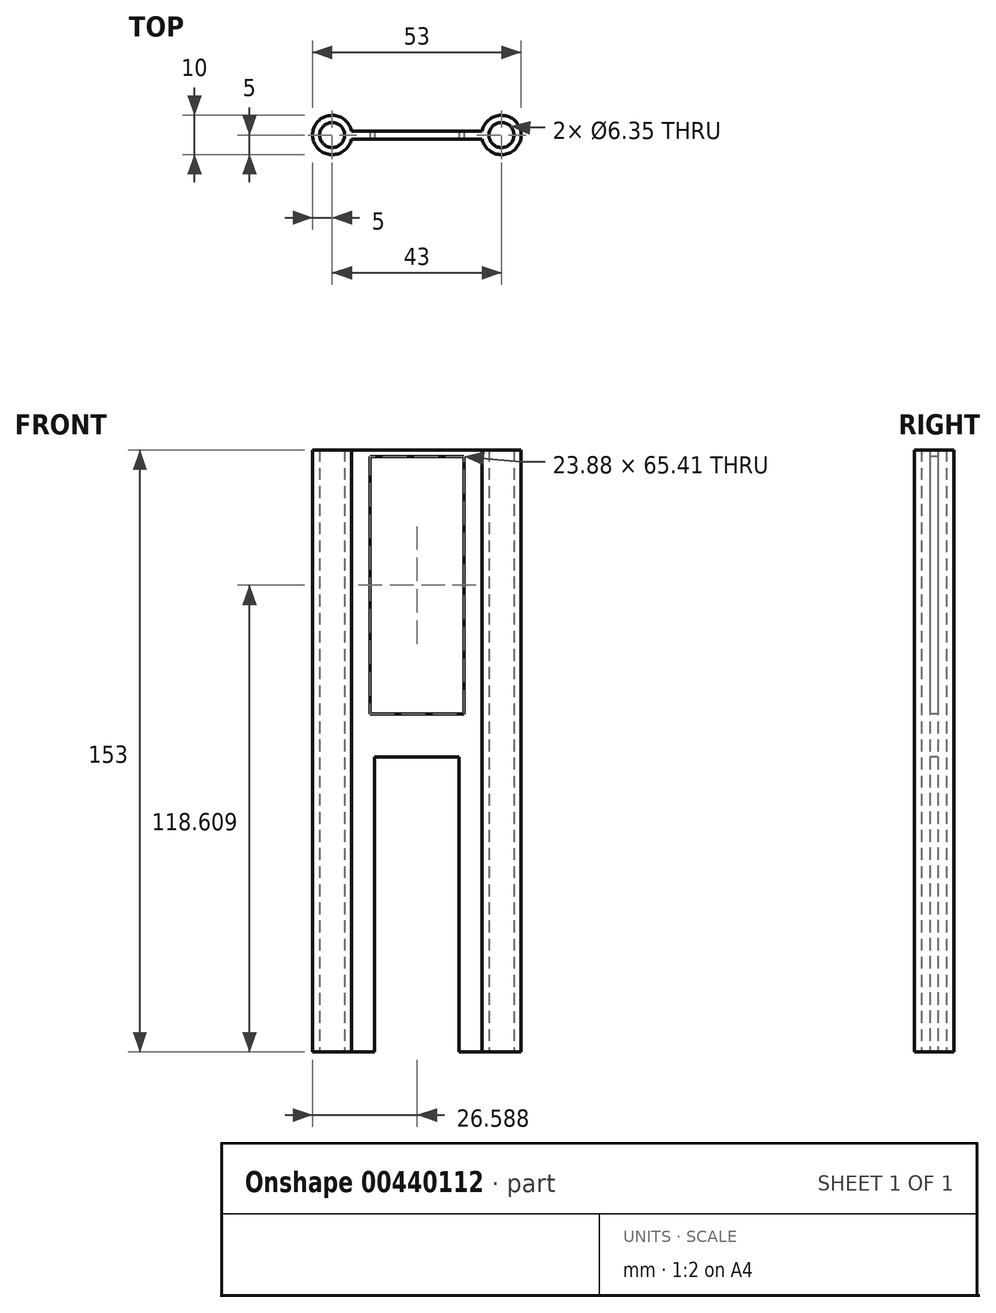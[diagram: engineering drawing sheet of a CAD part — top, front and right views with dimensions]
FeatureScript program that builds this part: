
annotation { "Feature Type Name" : "Feature", "Feature Type Description" : "" }
export const myFeature = defineFeature(function(context is Context, id is Id, definition is map)
    precondition{}
    {
        {
            var Q0;
            Q0=qCreatedBy(makeId("Top.planeOp"),FACE);
            var sketch = newSketch(context, id + "F0", { "sketchPlane" : qUnion([Q0])});
            skPoint(sketch, "E0.middle", {"position": v(0, 0) * mm});
            skLineSegment(sketch, "E1", {"start": v(0, 1) * mm, "end": v(0, -1) * mm, "construction": true});
            skPoint(sketch, "E2.endSnap0", {"position": v(26.5, 0) * mm});
            skPoint(sketch, "E3.endSnap0", {"position": v(-26.5, 0) * mm});
            skArc(sketch, "E4", {"start": v(16.6, -1) * mm, "mid": v(26.5, 0) * mm, "end": v(16.6, 1) * mm});
            skArc(sketch, "E5", {"start": v(-16.6, 1) * mm, "mid": v(-26.5, 0) * mm, "end": v(-16.6, -1) * mm});
            skCircle(sketch, "E6", {"center": v(21.5, 0) * mm, "radius": 3.17 * mm});
            skCircle(sketch, "E7", {"center": v(-21.5, 0) * mm, "radius": 3.17 * mm});
            skPoint(sketch, "E8.orphan", {"position": v(-26.5, 1) * mm});
            skPoint(sketch, "E9.orphan", {"position": v(-26.5, -1) * mm});
            skLineSegment(sketch, "E10.trimOffspring", {"start": v(16.6, 1) * mm, "end": v(-16.6, 1) * mm});
            skLineSegment(sketch, "E11.trimOffspring", {"start": v(16.6, -1) * mm, "end": v(-16.6, -1) * mm});
            skPoint(sketch, "E12.orphan", {"position": v(26.5, -1) * mm});
            skPoint(sketch, "E13.start.orphan", {"position": v(26.5, 1) * mm});
            skSolve(sketch);
        }
        {
            var Q0;
            Q0=makeQuery(id+"F0.imprint","IMPRINT",FACE,{"disambiguationData":[TD([[makeQuery(id+"F0.imprint","IMPRINT",EDGE,{"derivedFrom":sQuery(id+"F0.wireOp",EDGE,"E4")}),1.0]])]});
            extrude(context, id + "F1", {"entities" : qUnion([Q0]), "depth" : 153 * mm, "offsetDistance" : 25 * mm});
        }
        {
            var Q0;
            Q0=qCreatedBy(makeId("Front.planeOp"),FACE);
            var sketch = newSketch(context, id + "F2", { "sketchPlane" : qUnion([Q0])});
            skPoint(sketch, "E14.middle", {"position": v(0, 0) * mm});
            skLineSegment(sketch, "E15", {"start": v(-10.75, 0) * mm, "end": v(10.75, 0) * mm});
            skLineSegment(sketch, "E16", {"start": v(10.75, 0) * mm, "end": v(10.75, 75) * mm});
            skLineSegment(sketch, "E17", {"start": v(10.75, 75) * mm, "end": v(-10.75, 75) * mm});
            skLineSegment(sketch, "E18", {"start": v(-10.75, 75) * mm, "end": v(-10.75, 0) * mm});
            skLineSegment(sketch, "E19.bottom", {"start": v(-11.85, 151.31) * mm, "end": v(12.03, 151.31) * mm});
            skLineSegment(sketch, "E19.top", {"start": v(-11.85, 85.9) * mm, "end": v(12.03, 85.9) * mm});
            skLineSegment(sketch, "E19.left", {"start": v(-11.85, 151.31) * mm, "end": v(-11.85, 85.9) * mm});
            skLineSegment(sketch, "E19.right", {"start": v(12.03, 151.31) * mm, "end": v(12.03, 85.9) * mm});
            skSolve(sketch);
        }
        {
            var Q0;
            Q0 = qSketchRegion(id + "F2", true);
            extrude(context, id + "F3", {"entities" : qUnion([Q0]), "operationType" : NewBodyOperationType.REMOVE, "endBound" : BoundingType.SYMMETRIC, "oppositeDirection" : true, "depth" : 25 * mm, "offsetDistance" : 25 * mm});
        }
    });
